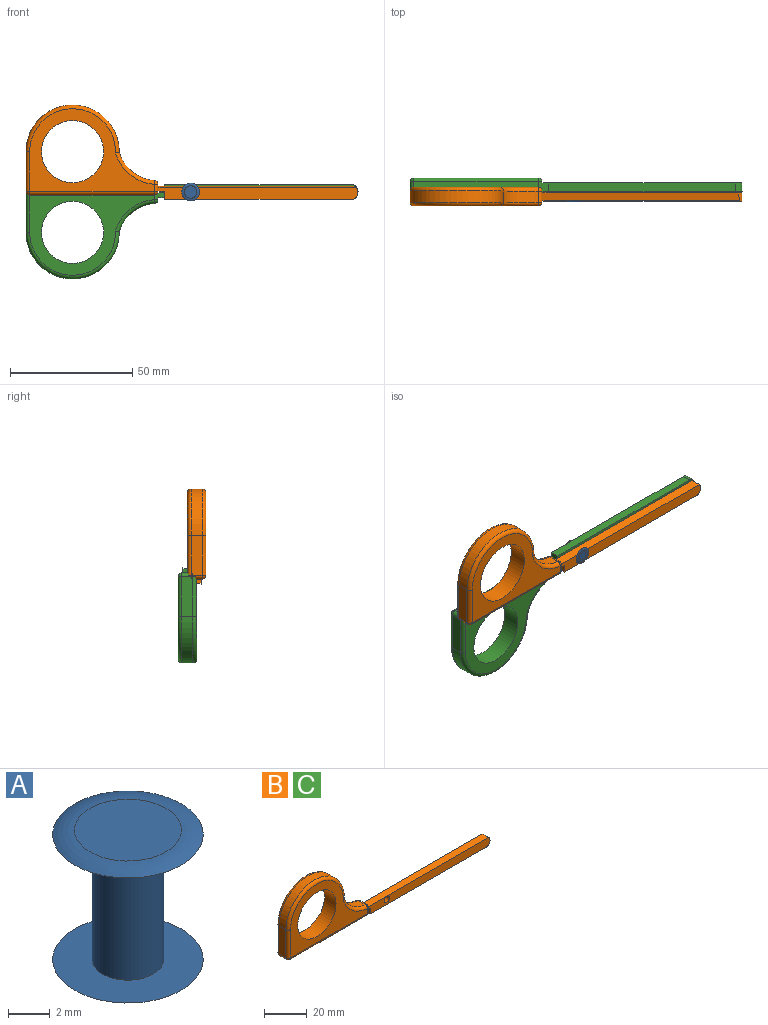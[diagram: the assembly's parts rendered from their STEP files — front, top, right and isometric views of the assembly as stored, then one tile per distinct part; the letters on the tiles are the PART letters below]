
ASSEMBLY  parts=3 mates=1
PART A: 7 faces, bbox 9.1x9.1x7.9 mm
  f0: plane 5.14x5.14mm, normal (0,0,1), area 20.8mm2, adj f5
  f1: plane 5.14x5.14mm, normal (0,0,-1), area 20.8mm2, adj f6
  f2: plane 7.24x7.24mm, normal (0,0,1), area 31.9mm2, adj f3,f6
  f3: cylinder r=1.71mm len=7.37mm, axis (0,0,-1), area 79.4mm2, adj f2,f4
  f4: plane 7.24x7.24mm, normal (0,0,-1), area 31.9mm2, adj f3,f5
  f5: torus R=2.57mm, axis (0,0,1), area 21.2mm2, adj f0,f4
  f6: torus R=2.57mm, axis (0,0,-1), area 21.2mm2, adj f1,f2
PART B: 35 faces, bbox 137.3x7.6x40.2 mm
  f0: cylinder r=2.79mm len=5.43mm, axis (0,1,0), area 25.5mm2, adj f1,f2,f5,f34
  f1: plane 81.79x4.83mm, normal (0,-1,0), area 374mm2, adj f0,f3,f4,f5,f6,f8,f34
  f2: plane 81.79x5.43mm, normal (0,1,0), area 422.8mm2, adj f0,f3,f4,f5,f6,f8,f34
  f3: plane 3.56x2.79mm, normal (0,0,-1), area 9.9mm2, adj f1,f2,f4,f7
  f4: plane 3.56x3.3mm, normal (-1,0,0), area 11.7mm2, adj f1,f2,f3,f5
  f5: plane 76.2x3.56mm, normal (0,0,-1), area 271mm2, adj f0,f1,f2,f4
  f6: cylinder r=1.71mm len=3.56mm, axis (0,1,0), area 38.3mm2, adj f1,f2
  f7: cylinder r=1.52mm len=4.57mm, axis (0,1,0), area 10.9mm2, adj f3,f8,f15,f20,f28
  f8: plane 4.57x2.87mm, normal (1,0,0), area 6.6mm2, adj f1,f2,f7,f9,f22,f30,f34
  f9: cylinder r=1.52mm len=4.57mm, axis (0,1,0), area 10.4mm2, adj f8,f10,f24,f32
  f10: cylinder r=16.51mm len=14.47mm, axis (0,1,0), area 89.9mm2, adj f9,f11,f25,f33
  f11: cylinder r=19.05mm len=38.1mm, axis (0,1,0), area 275mm2, adj f10,f12,f23,f31
  f12: plane 16.26x4.57mm, normal (-1,0,0), area 74.3mm2, adj f11,f13,f21,f29
  f13: cylinder r=1.52mm len=4.57mm, axis (0,1,0), area 10.9mm2, adj f12,f15,f19,f27
  f14: cylinder r=12.7mm len=25.4mm, axis (0,1,0), area 608mm2, adj f16,f17
  f15: plane 50.93x4.57mm, normal (0,0,-1), area 232.8mm2, adj f7,f13,f18,f26
  f16: plane 50.93x33.78mm, normal (0,-1,0), area 649.2mm2, adj f14,f26,f29,f30,f31,f33
  f17: plane 50.93x33.78mm, normal (0,1,0), area 649.2mm2, adj f14,f18,f21,f22,f23,f25
  f18: cylinder r=1.52mm len=50.93mm, axis (1,0,0), area 121.9mm2, adj f15,f17,f19,f20
  f19: sphere r=1.52mm, area 3.6mm2, adj f13,f18,f21
  f20: sphere r=1.52mm, area 3.6mm2, adj f7,f18,f22
  f21: cylinder r=1.52mm len=16.26mm, axis (0,0,-1), area 38.9mm2, adj f12,f17,f19,f23
  f22: cylinder r=1.52mm len=2.87mm, axis (0,0,1), area 6.9mm2, adj f8,f17,f20,f24
  f23: torus R=17.53mm, axis (0,-1,0), area 140mm2, adj f11,f17,f21,f25
  f24: sphere r=1.52mm, area 3.5mm2, adj f9,f22,f25
  f25: torus R=18.03mm, axis (0,-1,0), area 48.9mm2, adj f10,f17,f23,f24
  f26: cylinder r=1.52mm len=50.93mm, axis (-1,0,0), area 121.9mm2, adj f15,f16,f27,f28
  f27: sphere r=1.52mm, area 3.6mm2, adj f13,f26,f29
  f28: sphere r=1.52mm, area 3.6mm2, adj f7,f26,f30
  f29: cylinder r=1.52mm len=16.26mm, axis (0,0,1), area 38.9mm2, adj f12,f16,f27,f31
  f30: cylinder r=1.52mm len=2.87mm, axis (0,0,-1), area 6.9mm2, adj f8,f16,f28,f32
  f31: torus R=17.53mm, axis (0,-1,0), area 140mm2, adj f11,f16,f29,f33
  f32: sphere r=1.52mm, area 3.5mm2, adj f9,f30,f33
  f33: torus R=18.03mm, axis (0,-1,0), area 48.9mm2, adj f10,f16,f31,f32
  f34: plane 80.91x3.56mm, normal (0,-0.17,0.99), area 290.4mm2, adj f0,f1,f2,f8
PART C: same geometry as B
PLACE A rot(axis=(-1,0,0),90deg) t=(-1.63,-49.5,-25.84)mm fixed
PLACE B rot(axis=(0,1,0.01),0deg) t=(-65.77,-34.77,-21.09)mm
PLACE C rot(axis=(-1,0,0),180deg) t=(-65.77,-30.96,-30.59)mm fixed
MATE cylindrical B.f6 <-> A.f3  axis (0,1,0) through (-33.82,-36.54,-25.84)mm
